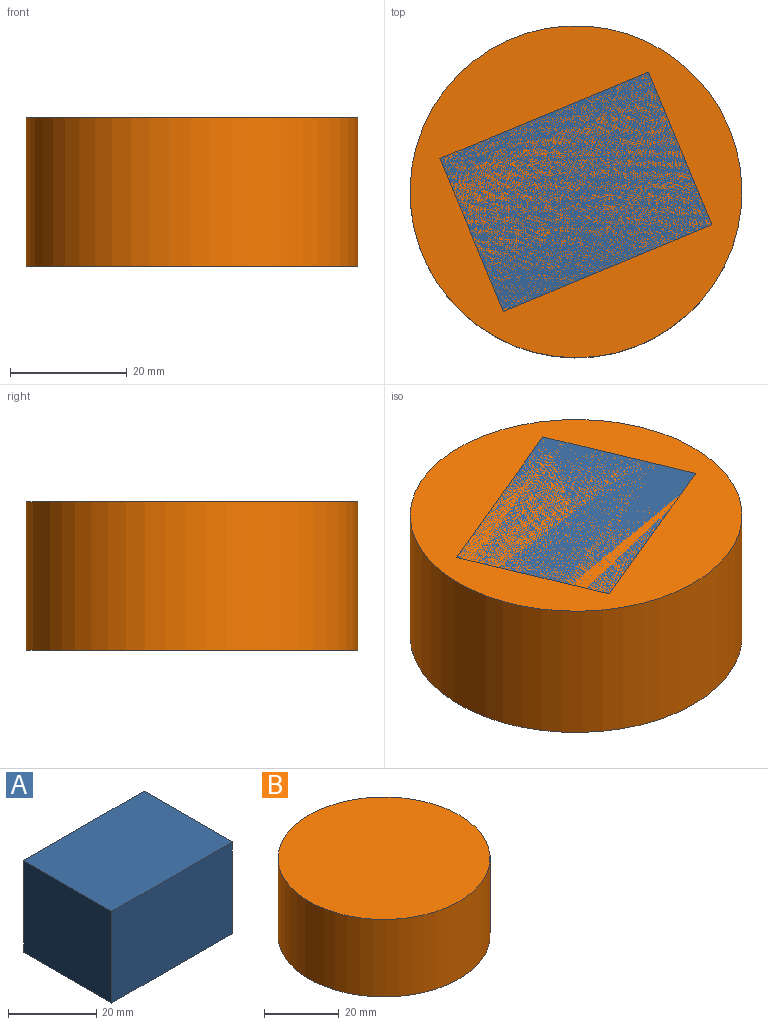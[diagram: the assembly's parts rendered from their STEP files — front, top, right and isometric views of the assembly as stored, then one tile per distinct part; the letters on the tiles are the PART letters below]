
ASSEMBLY  parts=2 mates=1
PART A: 6 faces, bbox 38.6x28.3x25.4 mm
  f0: plane 28.3x25.4mm, normal (-1,0,0), area 718.9mm2, adj f1,f3,f4,f5
  f1: plane 38.64x25.4mm, normal (0,-1,0), area 981.6mm2, adj f0,f2,f4,f5
  f2: plane 28.3x25.4mm, normal (1,0,0), area 718.9mm2, adj f1,f3,f4,f5
  f3: plane 38.64x25.4mm, normal (0,1,0), area 981.6mm2, adj f0,f2,f4,f5
  f4: plane 38.64x28.3mm, normal (0,0,1), area 1093.7mm2, adj f0,f1,f2,f3
  f5: plane 38.64x28.3mm, normal (0,0,-1), area 1093.7mm2, adj f0,f1,f2,f3
PART B: 3 faces, bbox 56.8x56.8x25.4 mm
  f0: cylinder r=28.4mm len=56.79mm, axis (0,0,-1), area 4531.7mm2, adj f1,f2
  f1: plane 56.79x56.79mm, normal (0,0,1), area 2533.1mm2, adj f0
  f2: plane 56.79x56.79mm, normal (0,0,-1), area 2533.1mm2, adj f0
PLACE A rot(axis=(0,0,-1),157.5deg) t=(17.35,81.38,52.25)mm
PLACE B rot(axis=(0.98,0.2,0),180deg) t=(23.36,47.93,77.65)mm
MATE fastened B.f0 <-> A.f4  axis (0,0,1) through (0.56,26.69,77.65)mm
